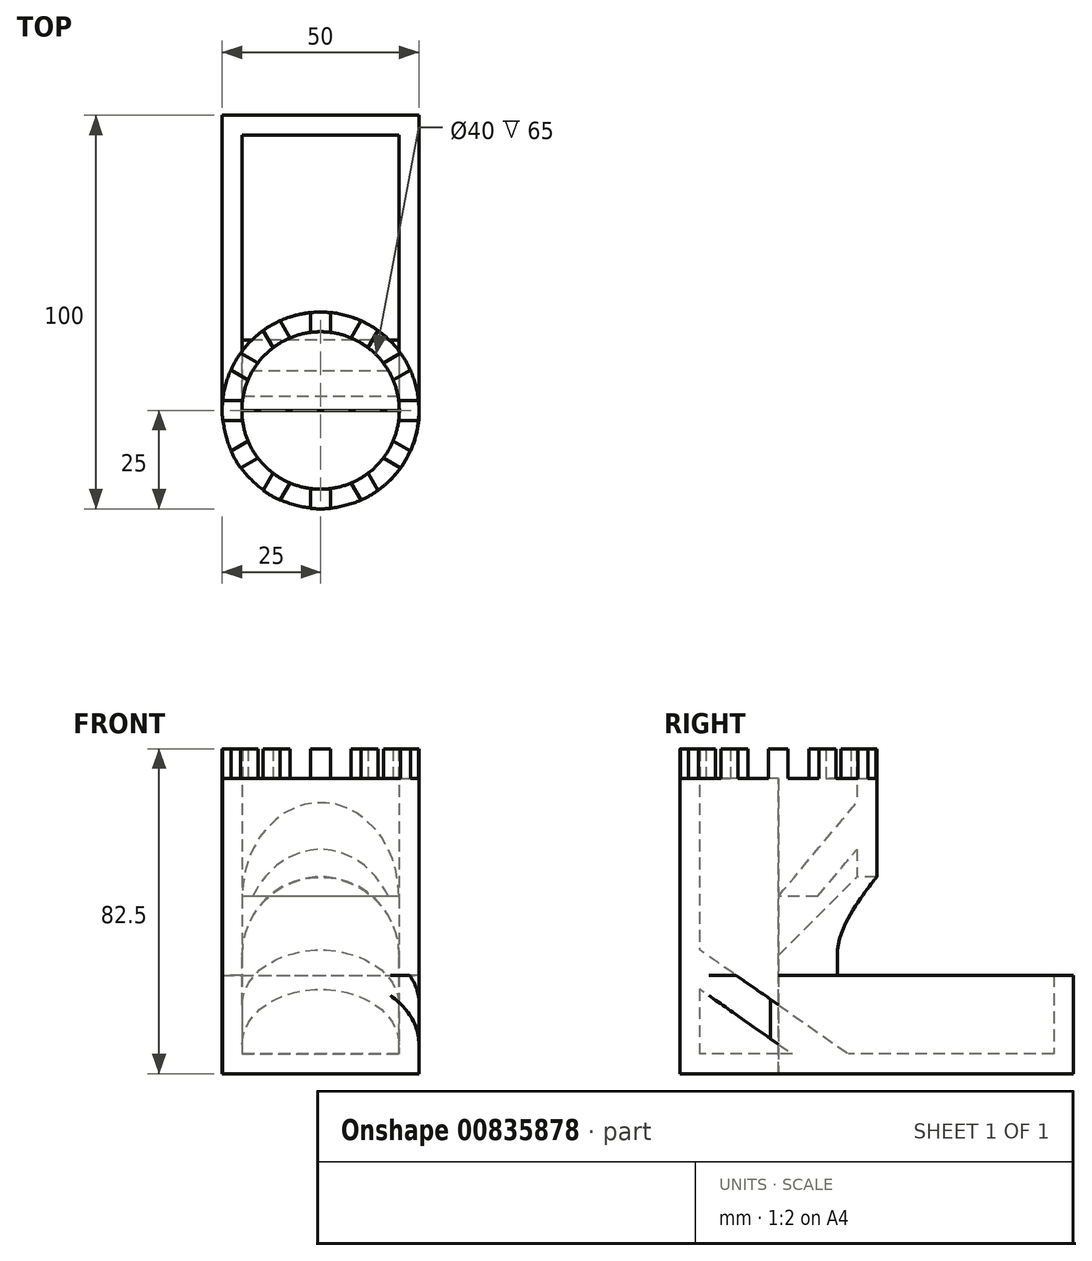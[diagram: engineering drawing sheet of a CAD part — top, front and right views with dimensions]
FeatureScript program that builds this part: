
annotation { "Feature Type Name" : "Feature", "Feature Type Description" : "" }
export const myFeature = defineFeature(function(context is Context, id is Id, definition is map)
    precondition{}
    {
        {
            var Q0;
            Q0=qCreatedBy(makeId("Right.planeOp"),FACE);
            var sketch = newSketch(context, id + "F0", { "sketchPlane" : qUnion([Q0])});
            skLineSegment(sketch, "E0", {"start": v(0, 0) * mm, "end": v(25, 0) * mm, "construction": true});
            skLineSegment(sketch, "E1", {"start": v(-25, 0) * mm, "end": v(0, 0) * mm, "construction": true});
            skLineSegment(sketch, "E2", {"start": v(-25, 0) * mm, "end": v(-25, 35) * mm, "construction": true});
            skLineSegment(sketch, "E3", {"start": v(-25, 35) * mm, "end": v(25, 0) * mm});
            skLineSegment(sketch, "E4", {"start": v(-25, 35) * mm, "end": v(-25, 25) * mm});
            skLineSegment(sketch, "E5", {"start": v(-25, 25) * mm, "end": v(10.71, 0) * mm});
            skLineSegment(sketch, "E6", {"start": v(10.71, 0) * mm, "end": v(25, 0) * mm});
            skLineSegment(sketch, "E7", {"start": v(0, 0) * mm, "end": v(0, 35) * mm, "construction": true});
            skLineSegment(sketch, "E8", {"start": v(0, 35) * mm, "end": v(25, 35) * mm, "construction": true});
            skLineSegment(sketch, "E9", {"start": v(25, 35) * mm, "end": v(25, 75) * mm, "construction": true});
            skLineSegment(sketch, "E10", {"start": v(0, 35) * mm, "end": v(0, 45) * mm, "construction": true});
            skLineSegment(sketch, "E11", {"start": v(0, 45) * mm, "end": v(25, 75) * mm});
            skLineSegment(sketch, "E12", {"start": v(0, 45) * mm, "end": v(10, 45) * mm});
            skLineSegment(sketch, "E13", {"start": v(10, 45) * mm, "end": v(25, 63) * mm});
            skLineSegment(sketch, "E14", {"start": v(25, 63) * mm, "end": v(25, 75) * mm});
            skSolve(sketch);
        }
        {
            var Q0;
            Q0=qCreatedBy(makeId("Top.planeOp"),FACE);
            var sketch = newSketch(context, id + "F1", { "sketchPlane" : qUnion([Q0])});
            skLineSegment(sketch, "E15.bottom", {"start": v(0, 0) * mm, "end": v(25, 0) * mm});
            skLineSegment(sketch, "E15.top", {"start": v(0, 75) * mm, "end": v(25, 75) * mm});
            skLineSegment(sketch, "E15.right", {"start": v(25, 0) * mm, "end": v(25, 75) * mm});
            skLineSegment(sketch, "E16.bottom", {"start": v(0, 0) * mm, "end": v(-25, 0) * mm});
            skLineSegment(sketch, "E16.top", {"start": v(0, 75) * mm, "end": v(-25, 75) * mm});
            skLineSegment(sketch, "E16.right", {"start": v(-25, 0) * mm, "end": v(-25, 75) * mm});
            skCircle(sketch, "E17", {"center": v(0, 0) * mm, "radius": 25 * mm});
            skSolve(sketch);
        }
        {
            var Q0;
            Q0 = qSketchRegion(id + "F1", true);
            extrude(context, id + "F2", {"entities" : qUnion([Q0]), "depth" : 5 * mm, "offsetDistance" : 25 * mm});
        }
        {
            var Q0;
            Q0=qCreatedBy(makeId("Top.planeOp"),FACE);
            var sketch = newSketch(context, id + "F3", { "sketchPlane" : qUnion([Q0])});
            skCircle(sketch, "E18", {"center": v(0, 0) * mm, "radius": 25 * mm});
            skCircle(sketch, "E19", {"center": v(0, 0) * mm, "radius": 20 * mm});
            skSolve(sketch);
        }
        {
            var Q0;
            Q0=makeQuery(id+"F3.imprint","IMPRINT",FACE,{"disambiguationData":[TD([[makeQuery(id+"F3.imprint","IMPRINT",EDGE,{"derivedFrom":sQuery(id+"F3.wireOp",EDGE,"E18")}),1.0]])]});
            extrude(context, id + "F4", {"entities" : qUnion([Q0]), "operationType" : NewBodyOperationType.ADD, "depth" : 75 * mm, "offsetDistance" : 25 * mm});
        }
        {
            var Q0;
            Q0=qCreatedBy(makeId("Top.planeOp"),FACE);
            var sketch = newSketch(context, id + "F5", { "sketchPlane" : qUnion([Q0])});
            skLineSegment(sketch, "E20", {"start": v(0, 0) * mm, "end": v(-25, 0) * mm, "construction": true});
            skLineSegment(sketch, "E21.bottom", {"start": v(-25, 0) * mm, "end": v(-20, 0) * mm});
            skLineSegment(sketch, "E21.top", {"start": v(-25, 75) * mm, "end": v(-20, 75) * mm});
            skLineSegment(sketch, "E21.left", {"start": v(-25, 0) * mm, "end": v(-25, 75) * mm});
            skLineSegment(sketch, "E21.right", {"start": v(-20, 0) * mm, "end": v(-20, 75) * mm});
            skLineSegment(sketch, "E22.bottom", {"start": v(-20, 75) * mm, "end": v(20, 75) * mm});
            skLineSegment(sketch, "E22.top", {"start": v(-20, 70) * mm, "end": v(20, 70) * mm});
            skLineSegment(sketch, "E22.left", {"start": v(-20, 75) * mm, "end": v(-20, 70) * mm});
            skLineSegment(sketch, "E22.right", {"start": v(20, 75) * mm, "end": v(20, 70) * mm});
            skLineSegment(sketch, "E23.left", {"start": v(20, 75) * mm, "end": v(20, 0) * mm});
            skLineSegment(sketch, "E24", {"start": v(20, 75) * mm, "end": v(25, 75) * mm});
            skLineSegment(sketch, "E25", {"start": v(25, 75) * mm, "end": v(25, 0) * mm});
            skLineSegment(sketch, "E26", {"start": v(25, 0) * mm, "end": v(20, 0) * mm});
            skSolve(sketch);
        }
        {
            var Q0;
            Q0 = qSketchRegion(id + "F5", true);
            extrude(context, id + "F6", {"entities" : qUnion([Q0]), "operationType" : NewBodyOperationType.ADD, "depth" : 25 * mm, "offsetDistance" : 25 * mm, "hasSecondDirection" : true, "secondDirectionOppositeDirection" : true, "secondDirectionDepth" : -5 * mm});
        }
        {
            var Q0;
            Q0=qCreatedBy(makeId("Front.planeOp"),FACE);
            var sketch = newSketch(context, id + "F7", { "sketchPlane" : qUnion([Q0])});
            skLineSegment(sketch, "E27.left", {"start": v(-20, 5) * mm, "end": v(-20, 30) * mm});
            skLineSegment(sketch, "E27.right", {"start": v(20, 5) * mm, "end": v(20, 30) * mm});
            skPoint(sketch, "E28", {"position": v(0, 30) * mm});
            skArc(sketch, "E29", {"start": v(20, 30) * mm, "mid": v(0, 50) * mm, "end": v(-20, 30) * mm});
            skLineSegment(sketch, "E30.top", {"start": v(-20, 5) * mm, "end": v(20, 5) * mm});
            skSolve(sketch);
        }
        {
            var Q0;
            Q0 = qSketchRegion(id + "F7", true);
            extrude(context, id + "F8", {"entities" : qUnion([Q0]), "operationType" : NewBodyOperationType.REMOVE, "oppositeDirection" : true, "depth" : 40.1 * mm, "offsetDistance" : 25 * mm});
        }
        {
            var Q0;
            Q0 = qSketchRegion(id + "F0", true);
            extrude(context, id + "F9", {"entities" : qUnion([Q0]), "operationType" : NewBodyOperationType.ADD, "depth" : 25 * mm, "offsetDistance" : 25 * mm, "hasSecondDirection" : true, "secondDirectionOppositeDirection" : true, "secondDirectionDepth" : 25 * mm});
        }
        {
            var Q0;
            Q0=qCreatedBy(makeId("Top.planeOp"),FACE);
            cPlane(context, id + "F10", {"entities" : qUnion([Q0]), "cplaneType" : CPlaneType.OFFSET, "offset" : 75 * mm, "width" : 150 * mm, "height" : 150 * mm});
        }
        {
            var Q0;
            Q0=qCreatedBy(id+"F10.planeOp",FACE);
            var sketch = newSketch(context, id + "F11", { "sketchPlane" : qUnion([Q0])});
            skCircle(sketch, "E31", {"center": v(0, 0) * mm, "radius": 25 * mm});
            skCircle(sketch, "E32", {"center": v(0, 0) * mm, "radius": 62.78 * mm});
            skSolve(sketch);
        }
        {
            var Q0;
            Q0=makeQuery(id+"F11.imprint","IMPRINT",FACE,{"disambiguationData":[TD([[makeQuery(id+"F11.imprint","IMPRINT",EDGE,{"derivedFrom":sQuery(id+"F11.wireOp",EDGE,"E31")}),-1.0]])]});
            extrude(context, id + "F12", {"entities" : qUnion([Q0]), "operationType" : NewBodyOperationType.REMOVE, "oppositeDirection" : true, "depth" : 50 * mm, "offsetDistance" : 25 * mm});
        }
        {
            var Q0;
            Q0=qCreatedBy(id+"F10.planeOp",FACE);
            var sketch = newSketch(context, id + "F13", { "sketchPlane" : qUnion([Q0])});
            skCircle(sketch, "E33", {"center": v(0.09, 0.09) * mm, "radius": 25 * mm});
            skCircle(sketch, "E34", {"center": v(0.09, 0.09) * mm, "radius": 62.78 * mm});
            skLineSegment(sketch, "E35", {"start": v(-73.62, 0) * mm, "end": v(78.49, 0) * mm});
            skSolve(sketch);
        }
        {
            var Q0;
            {var subQ0=sQuery(id+"F13.wireOp",EDGE,"E35");var subQ1=sQuery(id+"F13.wireOp",EDGE,"E33");var subQ2=makeQuery(id+"F13.imprint","INTERSECT",VERTEX,{"disambiguationData":[OD(0.0)],"derivedFrom":[subQ1,subQ0]});Q0=makeQuery(id+"F13.imprint","IMPRINT",FACE,{"disambiguationData":[TD([[makeQuery(id+"F13.imprint","IMPRINT",EDGE,{"disambiguationData":[TD([[subQ2,-1.0]])],"derivedFrom":subQ1}),-1.0]])]});}
            extrude(context, id + "F14", {"entities" : qUnion([Q0]), "operationType" : NewBodyOperationType.REMOVE, "oppositeDirection" : true, "depth" : 120.2 * mm, "offsetDistance" : 25 * mm});
        }
        {
            var Q0;
            Q0=qCreatedBy(id+"F10.planeOp",FACE);
            var sketch = newSketch(context, id + "F15", { "sketchPlane" : qUnion([Q0])});
            skCircle(sketch, "E36", {"center": v(0, 0) * mm, "radius": 25 * mm});
            skCircle(sketch, "E37", {"center": v(0, 0) * mm, "radius": 20 * mm});
            skLineSegment(sketch, "E38.bottom", {"start": v(-2.5, 0) * mm, "end": v(2.5, 0) * mm});
            skLineSegment(sketch, "E38.top", {"start": v(-2.5, 38.02) * mm, "end": v(2.5, 38.02) * mm});
            skLineSegment(sketch, "E38.left", {"start": v(-2.5, 0) * mm, "end": v(-2.5, 38.02) * mm});
            skLineSegment(sketch, "E38.right", {"start": v(2.5, 0) * mm, "end": v(2.5, 38.02) * mm});
            skSolve(sketch);
        }
        {
            var Q0;
            {var subQ0=sQuery(id+"F15.wireOp",EDGE,"E38.left");var subQ1=sQuery(id+"F15.wireOp",EDGE,"E36");var subQ2=makeQuery(id+"F15.imprint","INTERSECT",VERTEX,{"derivedFrom":[subQ1,subQ0]});Q0=makeQuery(id+"F15.imprint","IMPRINT",FACE,{"disambiguationData":[TD([[makeQuery(id+"F15.imprint","IMPRINT",EDGE,{"disambiguationData":[TD([[subQ2,1.0]])],"derivedFrom":subQ1}),1.0]])]});}
            extrude(context, id + "F16", {"entities" : qUnion([Q0]), "depth" : 7.5 * mm, "offsetDistance" : 25 * mm});
        }
        {
            var Q0;
            Q0=qCreatedBy(makeId("Front.planeOp"),FACE);
            var sketch = newSketch(context, id + "F17", { "sketchPlane" : qUnion([Q0])});
            skLineSegment(sketch, "E39", {"start": v(0, -70.6) * mm, "end": v(0, 97.62) * mm, "construction": true});
            skSolve(sketch);
        }
        {
            var Q0;
            Q0=makeQuery(id+"F16.opExtrude","SWEPT_BODY",BODY,{"disambiguationData":[OSD([sQuery(id+"F15.wireOp",EDGE,"E36"),sQuery(id+"F15.wireOp",EDGE,"E37"),sQuery(id+"F15.wireOp",EDGE,"E38.left"),sQuery(id+"F15.wireOp",EDGE,"E38.right")])]});
            var Q1;
            Q1=sQuery(id+"F17.wireOp",EDGE,"E39");
            circularPattern(context, id + "F18", {"operationType" : NewBodyOperationType.ADD, "entities" : qUnion([Q0]), "axis" : qUnion([Q1]), "angle" : 360 * degree, "instanceCount" : 12, "equalSpace" : true});
        }
    });
